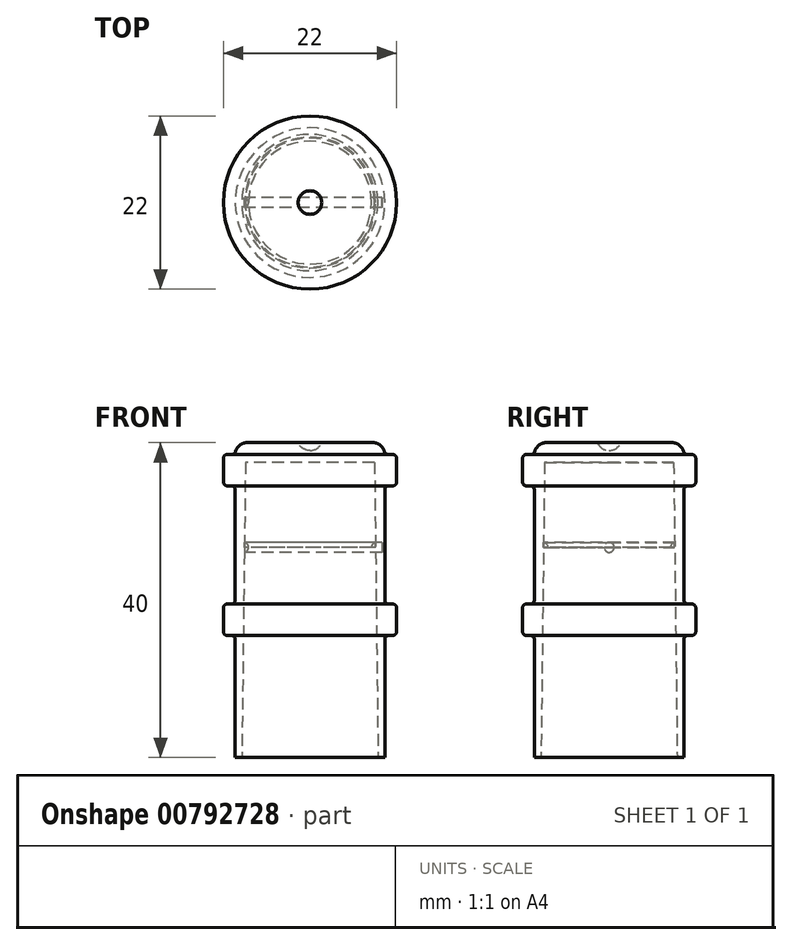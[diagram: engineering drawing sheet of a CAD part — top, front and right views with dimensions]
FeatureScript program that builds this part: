
annotation { "Feature Type Name" : "Feature", "Feature Type Description" : "" }
export const myFeature = defineFeature(function(context is Context, id is Id, definition is map)
    precondition{}
    {
        {
            var Q0;
            Q0=qCreatedBy(makeId("Front.planeOp"),FACE);
            var sketch = newSketch(context, id + "F0", { "sketchPlane" : qUnion([Q0])});
            skLineSegment(sketch, "E0", {"start": v(0, 32.02) * mm, "end": v(0, -23.37) * mm, "construction": true});
            skLineSegment(sketch, "E1", {"start": v(-8.65, -16.73) * mm, "end": v(-8.2, 20.77) * mm});
            skLineSegment(sketch, "E2", {"start": v(-8.2, 20.77) * mm, "end": v(0, 20.77) * mm});
            skLineSegment(sketch, "E3", {"start": v(-9.5, -16.73) * mm, "end": v(-9.5, -1.23) * mm});
            skLineSegment(sketch, "E4", {"start": v(-8, 23.27) * mm, "end": v(-1.5, 23.27) * mm});
            skPoint(sketch, "E5.visualSharp", {"position": v(-9.5, 23.27) * mm});
            skArc(sketch, "E5.filletArc", {"start": v(-8, 23.27) * mm, "mid": v(-9.06, 22.83) * mm, "end": v(-9.5, 21.77) * mm});
            skLineSegment(sketch, "E6.bottom", {"start": v(-9.5, 21.77) * mm, "end": v(-11, 21.77) * mm});
            skLineSegment(sketch, "E6.top", {"start": v(-9.5, 17.77) * mm, "end": v(-11, 17.77) * mm});
            skLineSegment(sketch, "E6.right", {"start": v(-11, 21.77) * mm, "end": v(-11, 17.77) * mm});
            skLineSegment(sketch, "E7.bottom", {"start": v(-9.5, 2.77) * mm, "end": v(-11, 2.77) * mm});
            skLineSegment(sketch, "E7.top", {"start": v(-9.5, -1.23) * mm, "end": v(-11, -1.23) * mm});
            skLineSegment(sketch, "E7.right", {"start": v(-11, 2.77) * mm, "end": v(-11, -1.23) * mm});
            skLineSegment(sketch, "E8.trimOffspring", {"start": v(-9.5, 2.77) * mm, "end": v(-9.5, 17.77) * mm});
            skArc(sketch, "E9", {"start": v(-1.5, 23.27) * mm, "mid": v(-0.9, 22.55) * mm, "end": v(0, 22.27) * mm});
            skLineSegment(sketch, "E10", {"start": v(-9.5, -16.73) * mm, "end": v(-8.65, -16.73) * mm});
            skLineSegment(sketch, "E11", {"start": v(0, 22.27) * mm, "end": v(0, 20.77) * mm});
            skLineSegment(sketch, "E12", {"start": v(-8.33, 9.97) * mm, "end": v(9.15, 9.97) * mm, "construction": true});
            skArc(sketch, "E13", {"start": v(-8.34, 9.33) * mm, "mid": v(-7.8, 9.97) * mm, "end": v(-8.32, 10.6) * mm});
            skLineSegment(sketch, "E14.bottom", {"start": v(-8.32, 10.6) * mm, "end": v(9.15, 10.6) * mm});
            skLineSegment(sketch, "E14.top", {"start": v(-8.32, 9.97) * mm, "end": v(9.15, 9.97) * mm});
            skLineSegment(sketch, "E14.left", {"start": v(-8.32, 10.6) * mm, "end": v(-8.32, 9.97) * mm});
            skLineSegment(sketch, "E14.right", {"start": v(9.15, 10.6) * mm, "end": v(9.15, 9.97) * mm});
            skSolve(sketch);
        }
        {
            var Q0;
            {var subQ0=sQuery(id+"F0.wireOp",EDGE,"E13");Q0=makeQuery(id+"F0.imprint","IMPRINT",FACE,{"disambiguationData":[TD([[makeQuery(id+"F0.imprint","IMPRINT",EDGE,{"derivedFrom":subQ0}),1.0]])]});}
            var Q1;
            {var subQ5=sQuery(id+"F0.wireOp",EDGE,"E2");Q1=makeQuery(id+"F0.imprint","IMPRINT",FACE,{"disambiguationData":[TD([[makeQuery(id+"F0.imprint","IMPRINT",EDGE,{"derivedFrom":subQ5}),1.0]])]});}
            var Q2;
            Q2=sQuery(id+"F0.wireOp",EDGE,"E0");
            revolve(context, id + "F1", {"surfaceOperationType" : NewSurfaceOperationType.NEW, "entities" : qUnion([Q0, Q1]), "axis" : qUnion([Q2]), "revolveType" : RevolveType.FULL});
        }
        {
            var Q0;
            Q0=makeQuery(id+"F1.opRevolve","SWEPT_EDGE",EDGE,{"disambiguationData":[OSD([sQuery(id+"F0.wireOp",EDGE,"E6.bottom"),sQuery(id+"F0.wireOp",EDGE,"E6.right")])]});
            var Q1;
            Q1=makeQuery(id+"F1.opRevolve","SWEPT_EDGE",EDGE,{"disambiguationData":[OSD([sQuery(id+"F0.wireOp",EDGE,"E6.top"),sQuery(id+"F0.wireOp",EDGE,"E6.right")])]});
            var Q2;
            Q2=makeQuery(id+"F1.opRevolve","SWEPT_EDGE",EDGE,{"disambiguationData":[OSD([sQuery(id+"F0.wireOp",EDGE,"E7.bottom"),sQuery(id+"F0.wireOp",EDGE,"E7.right")])]});
            var Q3;
            Q3=makeQuery(id+"F1.opRevolve","SWEPT_EDGE",EDGE,{"disambiguationData":[OSD([sQuery(id+"F0.wireOp",EDGE,"E7.top"),sQuery(id+"F0.wireOp",EDGE,"E7.right")])]});
            fillet(context, id + "F2", {"entities" : qUnion([Q0, Q1, Q2, Q3]), "radius" : 0.5 * mm, "tangentPropagation" : true, "allowEdgeOverflow" : false});
        }
        {
            var Q0;
            Q0=makeQuery(id+"F1.opRevolve","SWEPT_EDGE",EDGE,{"disambiguationData":[OSD([sQuery(id+"F0.wireOp",EDGE,"E6.top"),sQuery(id+"F0.wireOp",EDGE,"E8.trimOffspring")])]});
            var Q1;
            Q1=makeQuery(id+"F1.opRevolve","SWEPT_EDGE",EDGE,{"disambiguationData":[OSD([sQuery(id+"F0.wireOp",EDGE,"E7.bottom"),sQuery(id+"F0.wireOp",EDGE,"E8.trimOffspring")])]});
            var Q2;
            Q2=makeQuery(id+"F1.opRevolve","SWEPT_EDGE",EDGE,{"disambiguationData":[OSD([sQuery(id+"F0.wireOp",EDGE,"E5.filletArc"),sQuery(id+"F0.wireOp",EDGE,"E6.bottom")])]});
            var Q3;
            Q3=makeQuery(id+"F1.opRevolve","SWEPT_EDGE",EDGE,{"disambiguationData":[OSD([sQuery(id+"F0.wireOp",EDGE,"E3"),sQuery(id+"F0.wireOp",EDGE,"E7.top")])]});
            fillet(context, id + "F3", {"entities" : qUnion([Q0, Q1, Q2, Q3]), "radius" : 0.5 * mm, "tangentPropagation" : true, "allowEdgeOverflow" : false});
        }
        {
            var Q0;
            {var subQ0=sQuery(id+"F0.wireOp",EDGE,"E14.bottom");Q0=makeQuery(id+"F0.imprint","IMPRINT",FACE,{"disambiguationData":[TD([[makeQuery(id+"F0.imprint","IMPRINT",EDGE,{"derivedFrom":subQ0}),-1.0]])]});}
            var Q1;
            Q1=sQuery(id+"F0.wireOp",EDGE,"E14.top");
            revolve(context, id + "F4", {"surfaceOperationType" : NewSurfaceOperationType.NEW, "entities" : qUnion([Q0]), "axis" : qUnion([Q1]), "revolveType" : RevolveType.FULL});
        }
    });
